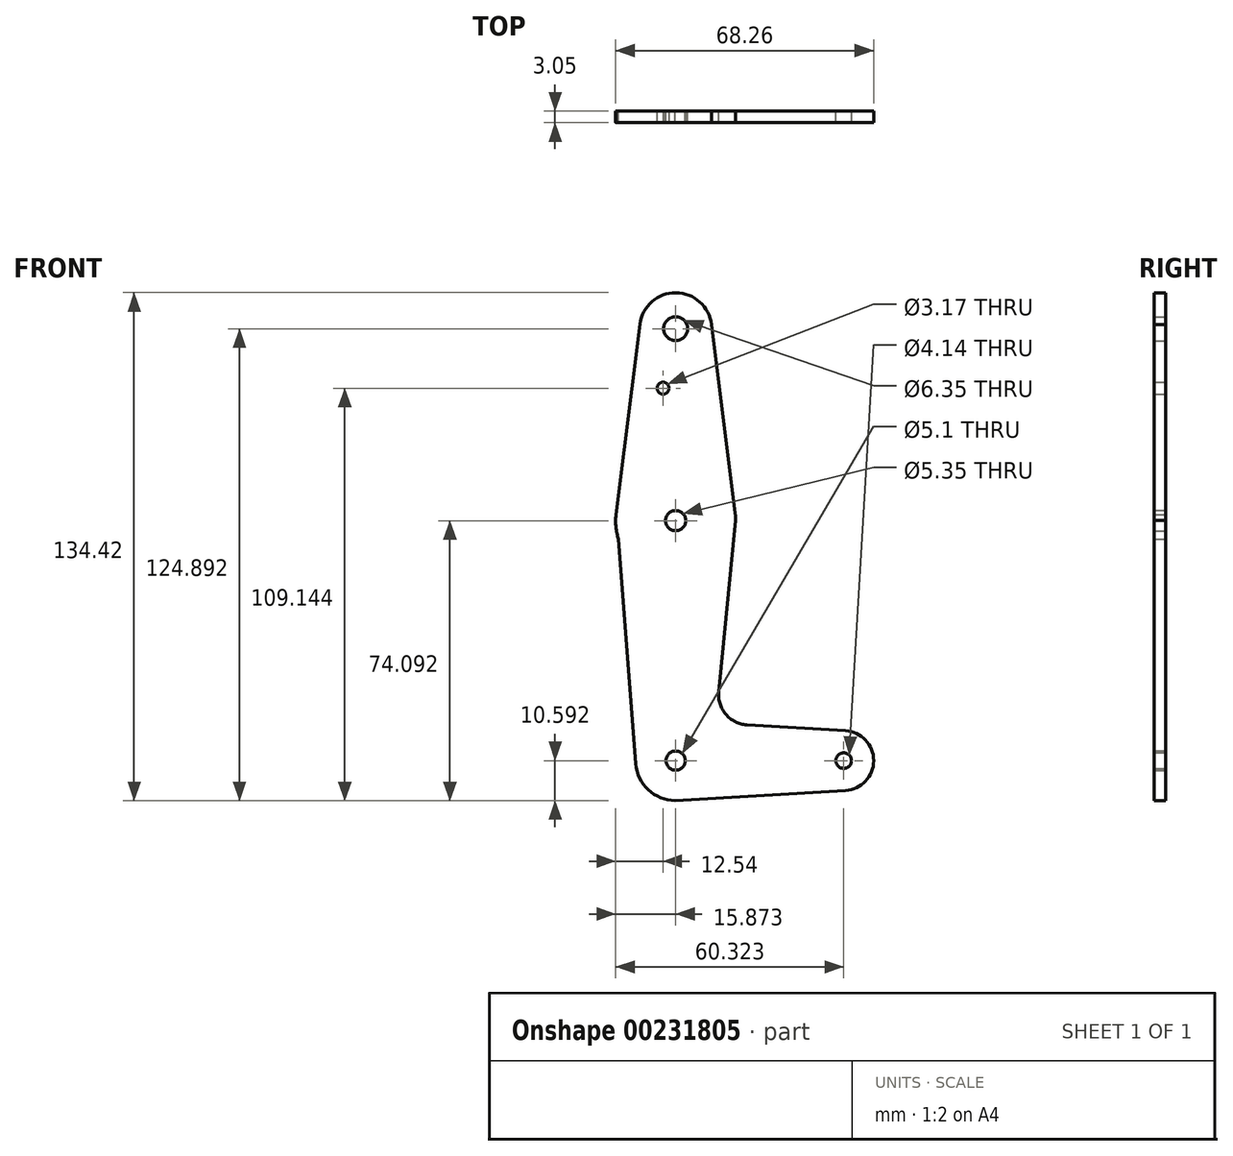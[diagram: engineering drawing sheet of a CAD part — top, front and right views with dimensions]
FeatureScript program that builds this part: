
annotation { "Feature Type Name" : "Feature", "Feature Type Description" : "" }
export const myFeature = defineFeature(function(context is Context, id is Id, definition is map)
    precondition{}
    {
        {
            var Q0;
            Q0=qCreatedBy(makeId("Front.planeOp"),FACE);
            var sketch = newSketch(context, id + "F0", { "sketchPlane" : qUnion([Q0])});
            skLineSegment(sketch, "E0", {"start": v(-23.05, 73.34) * mm, "end": v(-23.05, -40.96) * mm, "construction": true});
            skLineSegment(sketch, "E1", {"start": v(-23.05, -40.96) * mm, "end": v(21.4, -40.96) * mm, "construction": true});
            skCircle(sketch, "E2", {"center": v(-23.05, 73.34) * mm, "radius": 9.53 * mm});
            skCircle(sketch, "E3", {"center": v(-23.05, 22.54) * mm, "radius": 15.88 * mm});
            skCircle(sketch, "E4", {"center": v(-23.05, -40.96) * mm, "radius": 10.6 * mm});
            skCircle(sketch, "E5", {"center": v(21.4, -40.96) * mm, "radius": 7.94 * mm});
            skLineSegment(sketch, "E6", {"start": v(-7.17, 22.65) * mm, "end": v(-11.64, -22.77) * mm});
            skLineSegment(sketch, "E7", {"start": v(-4.2, -31.49) * mm, "end": v(21.87, -33.03) * mm});
            skLineSegment(sketch, "E8", {"start": v(-23.18, -51.55) * mm, "end": v(21.87, -48.88) * mm});
            skLineSegment(sketch, "E9", {"start": v(-38.15, 17.65) * mm, "end": v(-33.6, -41.77) * mm});
            skLineSegment(sketch, "E10", {"start": v(-38.85, 24.08) * mm, "end": v(-32.5, 74.53) * mm});
            skLineSegment(sketch, "E11", {"start": v(-13.58, 74.39) * mm, "end": v(-7.3, 24.53) * mm});
            skCircle(sketch, "E12", {"center": v(-23.05, 73.34) * mm, "radius": 3.18 * mm});
            skCircle(sketch, "E13", {"center": v(-23.05, 22.54) * mm, "radius": 2.67 * mm});
            skCircle(sketch, "E14", {"center": v(-23.05, -40.96) * mm, "radius": 2.55 * mm});
            skCircle(sketch, "E15", {"center": v(21.4, -40.96) * mm, "radius": 2.07 * mm});
            skCircle(sketch, "E16", {"center": v(-26.38, 57.6) * mm, "radius": 1.59 * mm});
            skArc(sketch, "E17.filletArc", {"start": v(-11.64, -22.77) * mm, "mid": v(-9.78, -28.71) * mm, "end": v(-4.2, -31.49) * mm});
            skSolve(sketch);
        }
        {
            var Q0;
            {var subQ0=sQuery(id+"F0.wireOp",EDGE,"E8");var subQ1=sQuery(id+"F0.wireOp",EDGE,"E4");var subQ2=makeQuery(id+"F0.imprint","INTERSECT",VERTEX,{"disambiguationData":[OD(0.0)],"derivedFrom":[subQ1,subQ0]});Q0=makeQuery(id+"F0.imprint","IMPRINT",FACE,{"disambiguationData":[TD([[makeQuery(id+"F0.imprint","IMPRINT",EDGE,{"disambiguationData":[TD([[subQ2,-1.0]])],"derivedFrom":subQ1}),1.0]])]});}
            var Q1;
            Q1=makeQuery(id+"F0.imprint","IMPRINT",FACE,{"disambiguationData":[TD([[makeQuery(id+"F0.imprint","IMPRINT",EDGE,{"derivedFrom":sQuery(id+"F0.wireOp",EDGE,"E12")}),-1.0]])]});
            var Q2;
            Q2=makeQuery(id+"F0.imprint","IMPRINT",FACE,{"disambiguationData":[TD([[makeQuery(id+"F0.imprint","IMPRINT",EDGE,{"derivedFrom":sQuery(id+"F0.wireOp",EDGE,"E15")}),-1.0]])]});
            var Q3;
            {var subQ0=sQuery(id+"F0.wireOp",EDGE,"E11");Q3=makeQuery(id+"F0.imprint","IMPRINT",FACE,{"disambiguationData":[TD([[makeQuery(id+"F0.imprint","IMPRINT",EDGE,{"derivedFrom":subQ0}),-1.0]])]});}
            var Q4;
            {var subQ5=sQuery(id+"F0.wireOp",EDGE,"E7");Q4=makeQuery(id+"F0.imprint","IMPRINT",FACE,{"disambiguationData":[TD([[makeQuery(id+"F0.imprint","IMPRINT",EDGE,{"derivedFrom":subQ5}),-1.0]])]});}
            var Q5;
            Q5=makeQuery(id+"F0.imprint","IMPRINT",FACE,{"disambiguationData":[TD([[makeQuery(id+"F0.imprint","IMPRINT",EDGE,{"derivedFrom":sQuery(id+"F0.wireOp",EDGE,"E14")}),-1.0]])]});
            var Q6;
            {var subQ0=sQuery(id+"F0.wireOp",EDGE,"E11");Q6=makeQuery(id+"F0.imprint","IMPRINT",FACE,{"disambiguationData":[TD([[makeQuery(id+"F0.imprint","IMPRINT",EDGE,{"derivedFrom":subQ0}),-1.0]])]});}
            var Q7;
            Q7=makeQuery(id+"F0.imprint","IMPRINT",FACE,{"disambiguationData":[TD([[makeQuery(id+"F0.imprint","IMPRINT",EDGE,{"derivedFrom":sQuery(id+"F0.wireOp",EDGE,"E13")}),-1.0]])]});
            extrude(context, id + "F1", {"entities" : qUnion([Q0, Q1, Q2, Q3, Q4, Q5, Q6, Q7]), "depth" : 3.05 * mm});
        }
    });
